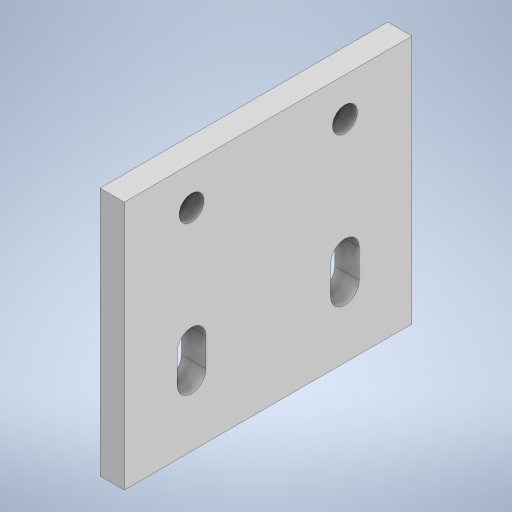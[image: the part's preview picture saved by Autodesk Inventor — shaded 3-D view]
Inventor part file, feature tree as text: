
AUTODESK INVENTOR PART (.ipt)
format: ipt  version: 2023 (Build 270158000, 158)  size: 223,744 bytes
history: native  units: mm
features: extrude x1, sketch x1
ambient origin geometry x8: Origin, YZ Plane, XZ Plane, XY Plane, X Axis, Y Axis, Z Axis, Center Point
bodies: Solid1 (feature_tree)
feature tree (2):
  extrude  "Extrusion1"  Depth=7.5mm
  sketch  "Sketch1"  dims[d1=75.0mm d4=7.5mm d5=7.5mm d8=13.75mm d10=40.0mm d12=6.35mm d13=0.0mm d15=10.0mm d16=6.5mm d17=6.5mm d18=30.75mm d19=65.0mm d20=7.5mm]
